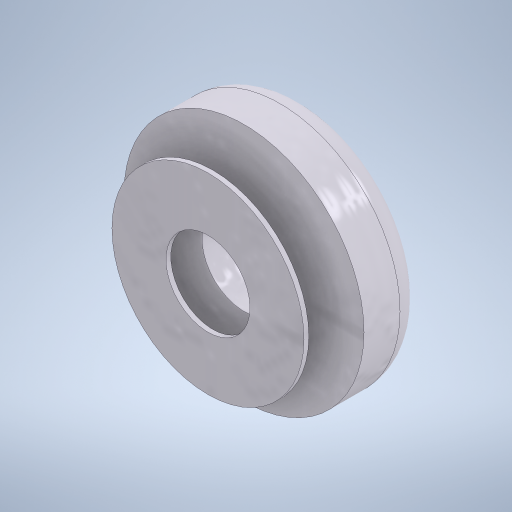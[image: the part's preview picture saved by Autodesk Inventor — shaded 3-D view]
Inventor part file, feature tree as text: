
AUTODESK INVENTOR PART (.ipt)
format: ipt  version: 2024.3 (Build 283343000, 343)  size: 294,912 bytes
history: native  units: mm
features: extrude x2, sketch x2, plane x1, fillet x1
ambient origin geometry x8: Origin, YZ Plane, XZ Plane, XY Plane, X Axis, Y Axis, Z Axis, Center Point
bodies: Solid1 (feature_tree)
feature tree (6):
  extrude  "Extrusion1"  Depth=10.0mm
  plane  "Work Plane1"
  extrude  "Extrusion2"  Depth=4.0mm
  fillet  "Fillet1"  Radius=8.0mm
  sketch  "Sketch1"  dims[d0=10.0mm d1=3.5mm]
  sketch  "Sketch2"  dims[d2=2.5mm d3=0.0mm d4=4.0mm d5=8.0mm d6=0.2mm d7=0.0mm d8=1.0mm]
